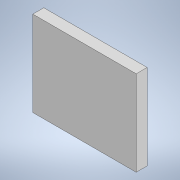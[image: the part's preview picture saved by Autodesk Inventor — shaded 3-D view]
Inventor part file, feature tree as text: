
AUTODESK INVENTOR PART (.ipt)
format: ipt  version: 2020 (Build 240168000, 168)  size: 87,040 bytes
history: native  units: mm
features: extrude x1, sketch x1
ambient origin geometry x8: Origin, YZ Plane, XZ Plane, XY Plane, X Axis, Y Axis, Z Axis, Center Point
bodies: Solid1 (feature_tree)
feature tree (2):
  extrude  "Extrusion1"  Depth=48.5mm
  sketch  "Sketch1"  dims[d0=5.15mm d1=48.5mm d2=40.0mm d3=0.0mm]
